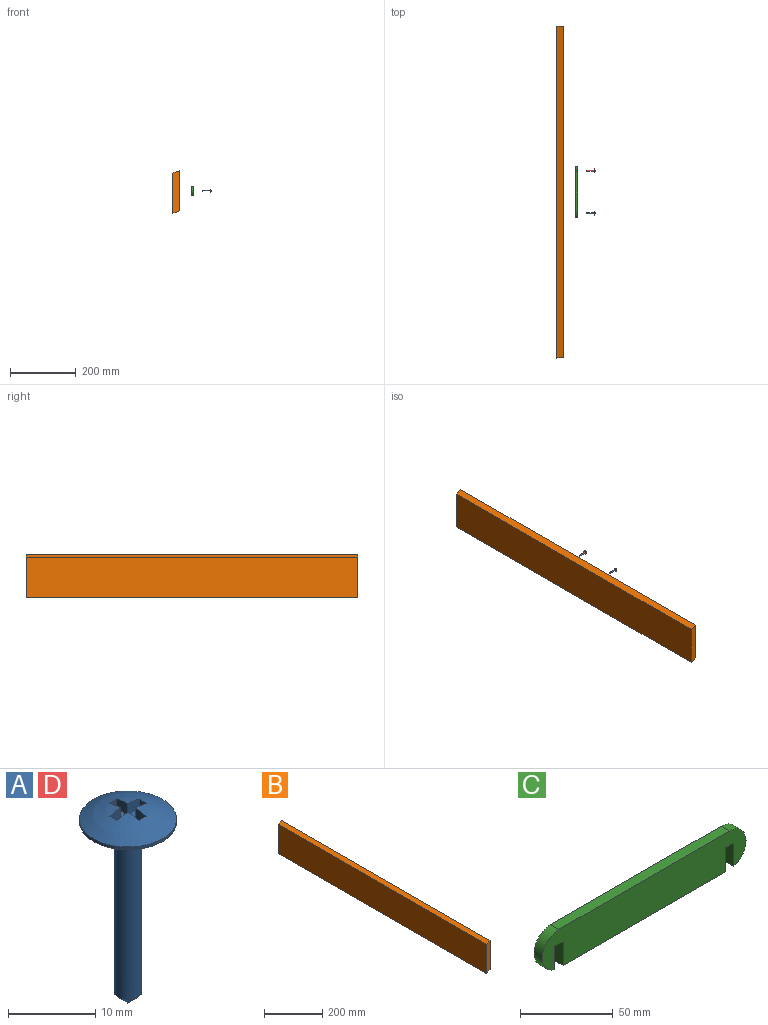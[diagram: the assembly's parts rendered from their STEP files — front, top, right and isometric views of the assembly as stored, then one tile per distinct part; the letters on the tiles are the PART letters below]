
ASSEMBLY  parts=4 mates=3
PART A: 18 faces, bbox 11.1x11.1x27.4 mm
  f0: sphere r=10.52mm, area 94.9mm2, adj f1,f5,f6,f7,f8,f9,f10,f11
  f1: cylinder r=5.56mm len=11.11mm, axis (0,0,-1), area 13.9mm2, adj f0,f2
  f2: plane 11.11x11.11mm, normal (0,0,-1), area 89.1mm2, adj f1,f3
  f3: cylinder r=1.59mm len=23.81mm, axis (0,0,-1), area 237.5mm2, adj f2,f4
  f4: cone r=1.59mm half-angle=45deg, axis (0,0,1), area 11.2mm2, adj f3
  f5: plane 1.31x1.19mm, normal (0,-1,0), area 1.6mm2, adj f0,f6,f16,f17
  f6: plane 1.79x1.55mm, normal (1,0,0), area 2.6mm2, adj f0,f5,f7,f17
  f7: plane 1.79x1.55mm, normal (0,-1,0), area 2.6mm2, adj f0,f6,f8,f17
  f8: plane 1.31x1.19mm, normal (1,0,0), area 1.6mm2, adj f0,f7,f9,f17
  f9: plane 1.79x1.55mm, normal (0,1,0), area 2.6mm2, adj f0,f8,f10,f17
  f10: plane 1.79x1.55mm, normal (1,0,0), area 2.6mm2, adj f0,f9,f11,f17
  f11: plane 1.31x1.19mm, normal (0,1,0), area 1.6mm2, adj f0,f10,f12,f17
  f12: plane 1.79x1.55mm, normal (-1,0,0), area 2.6mm2, adj f0,f11,f13,f17
  f13: plane 1.79x1.55mm, normal (0,1,0), area 2.6mm2, adj f0,f12,f14,f17
  f14: plane 1.31x1.19mm, normal (-1,0,0), area 1.6mm2, adj f0,f13,f15,f17
  f15: plane 1.79x1.55mm, normal (0,-1,0), area 2.6mm2, adj f0,f14,f16,f17
  f16: plane 1.79x1.55mm, normal (-1,0,0), area 2.6mm2, adj f0,f5,f15,f17
  f17: plane 4.76x4.76mm, normal (0,0,1), area 9.9mm2, adj f5,f6,f7,f8,f9,f10,f11,f12
PART B: 10 faces, bbox 19.1x1012.8x129.8 mm
  f0: plane 1012.83x122.82mm, normal (1,0,0), area 124371.6mm2, adj f1,f3,f4,f5,f7,f9
  f1: plane 129.75x19.05mm, normal (0,1,0), area 2339.7mm2, adj f0,f2,f3,f4
  f2: plane 1012.83x122.82mm, normal (-1,0,0), area 124396.3mm2, adj f1,f3,f4,f5
  f3: plane 1012.83x19.05mm, normal (-0.34,0,0.94), area 20532.6mm2, adj f0,f1,f2,f5
  f4: plane 1012.83x19.05mm, normal (0.34,0,-0.94), area 20532.6mm2, adj f0,f1,f2,f5
  f5: plane 129.75x19.05mm, normal (0,-1,0), area 2339.7mm2, adj f0,f2,f3,f4
  f6: cone r=0mm half-angle=59deg, axis (1,0,0), area 14.4mm2, adj f7
  f7: cylinder r=1.98mm len=12.7mm, axis (1,0,0), area 158.3mm2, adj f0,f6
  f8: cone r=0mm half-angle=59deg, axis (1,0,0), area 14.4mm2, adj f9
  f9: cylinder r=1.98mm len=12.7mm, axis (1,0,0), area 158.3mm2, adj f0,f8
PART C: 12 faces, bbox 155.6x6.4x25.4 mm
  f0: plane 123.83x6.35mm, normal (0,0,-1), area 786.3mm2, adj f1,f9,f10,f11
  f1: plane 15.88x6.35mm, normal (1,0,0), area 100.8mm2, adj f0,f2,f10,f11
  f2: plane 6.35x6.35mm, normal (0,0,-1), area 40.3mm2, adj f1,f3,f10,f11
  f3: plane 15.47x6.35mm, normal (-1,0,0), area 98.2mm2, adj f2,f4,f10,f11
  f4: cylinder r=12.7mm len=25mm, axis (0,1,0), area 233mm2, adj f3,f5,f10,f11
  f5: plane 130.18x6.35mm, normal (0,0,1), area 826.6mm2, adj f4,f6,f10,f11
  f6: cylinder r=12.7mm len=25mm, axis (0,1,0), area 233mm2, adj f5,f7,f10,f11
  f7: plane 15.47x6.35mm, normal (1,0,0), area 98.2mm2, adj f6,f8,f10,f11
  f8: plane 6.35x6.35mm, normal (0,0,-1), area 40.3mm2, adj f7,f9,f10,f11
  f9: plane 15.88x6.35mm, normal (-1,0,0), area 100.8mm2, adj f0,f8,f10,f11
  f10: plane 155.58x25.4mm, normal (0,-1,0), area 3612.4mm2, adj f0,f1,f2,f3,f4,f5,f6,f7
  f11: plane 155.58x25.4mm, normal (0,1,0), area 3612.4mm2, adj f0,f1,f2,f3,f4,f5,f6,f7
PART D: same geometry as A
PLACE A rot(axis=(0,1,0),90deg) t=(117.87,-63.5,30.96)mm
PLACE B at identity fixed
PLACE C rot(axis=(0.71,0.71,0),180deg) t=(66.68,1.59,0)mm
PLACE D rot(axis=(0,1,0),90deg) t=(117.87,66.68,30.96)mm
MATE fastened B.f8 <-> C.f4  axis (1,0,0) through (22.22,66.68,0)mm
MATE fastened D.f1 <-> C.f4  axis (-1,0,0) through (117.48,66.68,0)mm
MATE fastened A.f1 <-> C.f6  axis (-1,0,0) through (117.48,-63.5,0)mm
